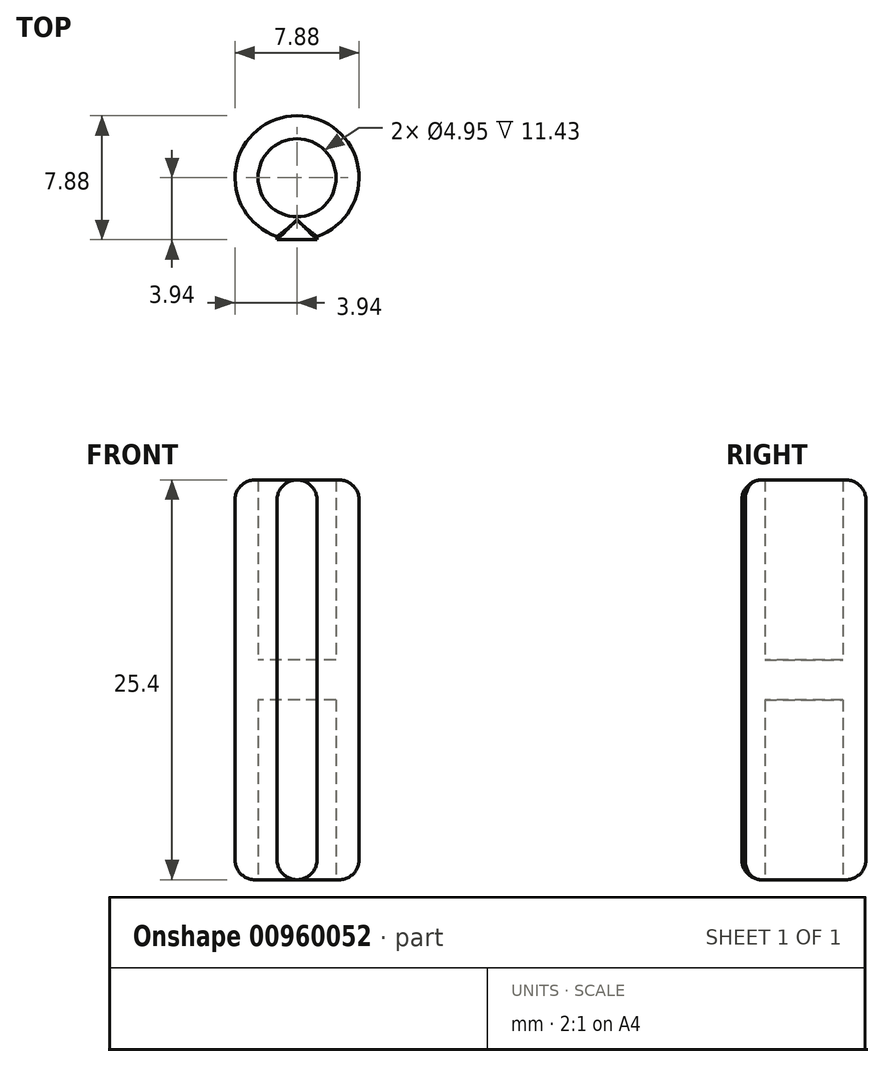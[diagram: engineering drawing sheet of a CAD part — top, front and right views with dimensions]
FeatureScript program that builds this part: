
annotation { "Feature Type Name" : "Feature", "Feature Type Description" : "" }
export const myFeature = defineFeature(function(context is Context, id is Id, definition is map)
    precondition{}
    {
        {
            var Q0;
            Q0=qCreatedBy(makeId("Top.planeOp"),FACE);
            var sketch = newSketch(context, id + "F0", { "sketchPlane" : qUnion([Q0])});
            skCircle(sketch, "E0", {"center": v(0, 0) * mm, "radius": 2.48 * mm});
            skCircle(sketch, "E1", {"center": v(0, 0) * mm, "radius": 3.94 * mm});
            skLineSegment(sketch, "E2", {"start": v(0, -3.94) * mm, "end": v(1.27, -3.94) * mm});
            skLineSegment(sketch, "E3", {"start": v(1.27, -3.94) * mm, "end": v(1.27, -3.73) * mm});
            skLineSegment(sketch, "E4", {"start": v(0, -3.94) * mm, "end": v(-1.27, -3.94) * mm});
            skLineSegment(sketch, "E5", {"start": v(-1.27, -3.94) * mm, "end": v(-1.27, -3.73) * mm});
            skSolve(sketch);
        }
        {
            var Q0;
            Q0=makeQuery(id+"F0.imprint","IMPRINT",FACE,{"disambiguationData":[TD([[makeQuery(id+"F0.imprint","IMPRINT",EDGE,{"derivedFrom":sQuery(id+"F0.wireOp",EDGE,"E0")}),-1.0]])]});
            var Q1;
            {var subQ0=sQuery(id+"F0.wireOp",EDGE,"E4");Q1=makeQuery(id+"F0.imprint","IMPRINT",FACE,{"disambiguationData":[TD([[makeQuery(id+"F0.imprint","IMPRINT",EDGE,{"derivedFrom":subQ0}),-1.0]])]});}
            var Q2;
            {var subQ0=sQuery(id+"F0.wireOp",EDGE,"E2");Q2=makeQuery(id+"F0.imprint","IMPRINT",FACE,{"disambiguationData":[TD([[makeQuery(id+"F0.imprint","IMPRINT",EDGE,{"derivedFrom":subQ0}),1.0]])]});}
            extrude(context, id + "F1", {"entities" : qUnion([Q0, Q1, Q2]), "endBound" : BoundingType.SYMMETRIC, "depth" : 25.4 * mm, "offsetDistance" : 25.4 * mm});
        }
        {
            var Q0;
            Q0=makeQuery(id+"F0.imprint","IMPRINT",FACE,{"disambiguationData":[TD([[makeQuery(id+"F0.imprint","IMPRINT",EDGE,{"derivedFrom":sQuery(id+"F0.wireOp",EDGE,"E0")}),1.0]])]});
            extrude(context, id + "F2", {"entities" : qUnion([Q0]), "operationType" : NewBodyOperationType.ADD, "endBound" : BoundingType.SYMMETRIC, "depth" : 2.54 * mm, "offsetDistance" : 25.4 * mm});
        }
        {
            var Q0;
            Q0=makeQuery(id+"F1.opExtrude","CAP_EDGE",EDGE,{"disambiguationData":[OSD([sQuery(id+"F0.wireOp",EDGE,"E1")])],"isStart":false});
            var Q1;
            Q1=makeQuery(id+"F1.opExtrude","CAP_EDGE",EDGE,{"disambiguationData":[OSD([sQuery(id+"F0.wireOp",EDGE,"E1")])],"isStart":true});
            var Q2;
            Q2=makeQuery(id+"F1.opExtrude","CAP_EDGE",EDGE,{"disambiguationData":[OSD([sQuery(id+"F0.wireOp",EDGE,"E2"),sQuery(id+"F0.wireOp",EDGE,"E4")])],"isStart":false});
            var Q3;
            Q3=makeQuery(id+"F1.opExtrude","CAP_EDGE",EDGE,{"disambiguationData":[OSD([sQuery(id+"F0.wireOp",EDGE,"E3")])],"isStart":false});
            var Q4;
            Q4=makeQuery(id+"F1.opExtrude","CAP_EDGE",EDGE,{"disambiguationData":[OSD([sQuery(id+"F0.wireOp",EDGE,"E5")])],"isStart":false});
            var Q5;
            Q5=makeQuery(id+"F1.opExtrude","CAP_EDGE",EDGE,{"disambiguationData":[OSD([sQuery(id+"F0.wireOp",EDGE,"E3")])],"isStart":true});
            var Q6;
            Q6=makeQuery(id+"F1.opExtrude","CAP_EDGE",EDGE,{"disambiguationData":[OSD([sQuery(id+"F0.wireOp",EDGE,"E2"),sQuery(id+"F0.wireOp",EDGE,"E4")])],"isStart":true});
            var Q7;
            Q7=makeQuery(id+"F1.opExtrude","CAP_EDGE",EDGE,{"disambiguationData":[OSD([sQuery(id+"F0.wireOp",EDGE,"E5")])],"isStart":true});
            fillet(context, id + "F3", {"entities" : qUnion([Q0, Q1, Q2, Q3, Q4, Q5, Q6, Q7]), "radius" : 1.27 * mm, "tangentPropagation" : true, "allowEdgeOverflow" : false});
        }
    });
